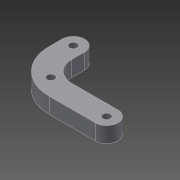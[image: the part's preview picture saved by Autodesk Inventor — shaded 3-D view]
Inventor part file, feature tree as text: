
AUTODESK INVENTOR PART (.ipt)
format: ipt  version: 2014 SP1 (Build 180222100, 222)  size: 91,648 bytes
history: native  units: in
note: dims shown in document units (in); Inventor stores cm internally (conversion verified against a paired STEP export)
features: hole x3, other x3, extrude x1, sketch x1
ambient origin geometry x5: Origin, X Axis, Y Axis, Z Axis, Center Point
bodies: Solid1 (feature_tree)
feature tree (8):
  extrude  "Extrusion1"  Depth=0.125in
  hole  "Hole1"  [1 undecoded]
  hole  "Hole2"  [1 undecoded]
  hole  "Hole3"  [1 undecoded]
  other  "Right (YZ)"
  other  "Top (XZ)"
  other  "Front (XY)"
  sketch  "Sketch1"  dims[d0=0.125in d1=0.0in d2=1.0in d3=1.0in d4=0.0625in d5=0.75in d6=0.375in d7=0.25in d8=0.5635in d9=1.0in d10=0.8108in d11=1.0in d12=1.0in d13=0.0625in d14=0.75in d15=0.375in d16=0.25in d17=0.5635in d18=1.0in d19=0.8108in d20=1.0in d21=1.0in d22=0.0625in d23=0.75in d24=0.375in d25=0.25in d26=0.5635in d27=1.0in d28=0.8108in]
note: 3 required parameter values undecoded (feature->parameter linkage not recoverable at this tier; creation-order binding heuristic only, values carry confidence <= 0.55)
